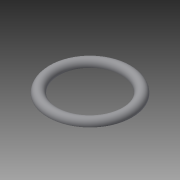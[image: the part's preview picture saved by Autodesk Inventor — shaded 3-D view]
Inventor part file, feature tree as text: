
AUTODESK INVENTOR PART (.ipt)
format: ipt  version: 2015 (Build 190159000, 159)  size: 126,976 bytes
history: native  units: in
note: dims shown in document units (in); Inventor stores cm internally (conversion verified against a paired STEP export)
features: sketch x2, revolve x1, extrude x1
ambient origin geometry x8: Origin, YZ Plane, XZ Plane, XY Plane, X Axis, Y Axis, Z Axis, Center Point
bodies: Body1 (feature_tree)
feature tree (4):
  revolve  "Revolution2"  [1 undecoded]
  extrude  "Extrusion2"  [1 undecoded]
  sketch  "Sketch3"  dims[d6=90.0deg d12=0.0in d13=0.0in]
  sketch  "Sketch5"
note: 2 required parameter values undecoded (feature->parameter linkage not recoverable at this tier; creation-order binding heuristic only, values carry confidence <= 0.55)